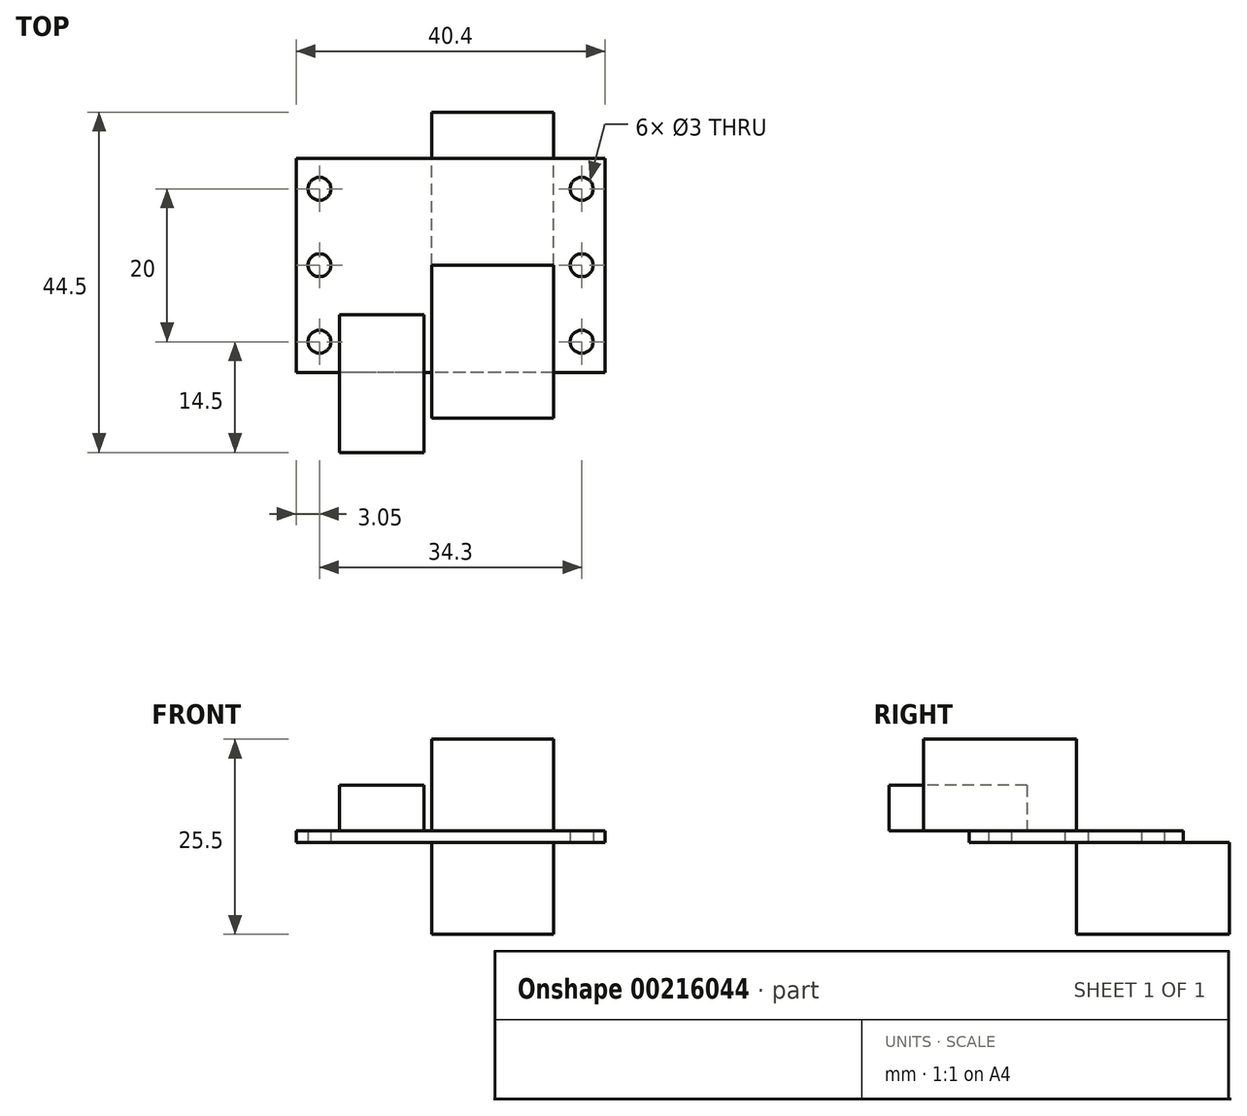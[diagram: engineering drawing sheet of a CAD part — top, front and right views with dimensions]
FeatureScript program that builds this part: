
annotation { "Feature Type Name" : "Feature", "Feature Type Description" : "" }
export const myFeature = defineFeature(function(context is Context, id is Id, definition is map)
    precondition{}
    {
        {
            var Q0;
            Q0=qCreatedBy(makeId("Top.planeOp"),FACE);
            var sketch = newSketch(context, id + "F0", { "sketchPlane" : qUnion([Q0])});
            skLineSegment(sketch, "E0.bottom", {"start": v(20.2, -14) * mm, "end": v(-20.2, -14) * mm});
            skLineSegment(sketch, "E0.top", {"start": v(20.2, 14) * mm, "end": v(-20.2, 14) * mm});
            skLineSegment(sketch, "E0.left", {"start": v(20.2, -14) * mm, "end": v(20.2, 14) * mm});
            skLineSegment(sketch, "E0.right", {"start": v(-20.2, -14) * mm, "end": v(-20.2, 14) * mm});
            skPoint(sketch, "E0.middle", {"position": v(0, 0) * mm});
            skCircle(sketch, "E1", {"center": v(-17.15, 0) * mm, "radius": 1.5 * mm});
            skCircle(sketch, "E2", {"center": v(17.15, 0) * mm, "radius": 1.5 * mm});
            skCircle(sketch, "E3", {"center": v(17.15, 10) * mm, "radius": 1.5 * mm});
            skCircle(sketch, "E4", {"center": v(17.15, -10) * mm, "radius": 1.5 * mm});
            skCircle(sketch, "E5", {"center": v(-17.15, 10) * mm, "radius": 1.5 * mm});
            skCircle(sketch, "E6", {"center": v(-17.15, -10) * mm, "radius": 1.5 * mm});
            skLineSegment(sketch, "E7", {"start": v(0, -9.21) * mm, "end": v(0, 7.96) * mm, "construction": true});
            skLineSegment(sketch, "E8", {"start": v(-9.5, 0) * mm, "end": v(8.49, 0) * mm, "construction": true});
            skSolve(sketch);
        }
        {
            var Q0;
            Q0 = qSketchRegion(id + "F0", true);
            extrude(context, id + "F1", {"entities" : qUnion([Q0]), "depth" : 1.5 * mm});
        }
        {
            var Q0;
            Q0=makeQuery(id+"F1.opExtrude","CAP_FACE",FACE,{"disambiguationData":[OSD([sQuery(id+"F0.wireOp",EDGE,"E0.bottom"),sQuery(id+"F0.wireOp",EDGE,"E0.top"),sQuery(id+"F0.wireOp",EDGE,"E0.left"),sQuery(id+"F0.wireOp",EDGE,"E0.right"),sQuery(id+"F0.wireOp",EDGE,"E1"),sQuery(id+"F0.wireOp",EDGE,"E2"),sQuery(id+"F0.wireOp",EDGE,"E3"),sQuery(id+"F0.wireOp",EDGE,"E4"),sQuery(id+"F0.wireOp",EDGE,"E5"),sQuery(id+"F0.wireOp",EDGE,"E6")])],"isStart":false});
            var sketch = newSketch(context, id + "F2", { "sketchPlane" : qUnion([Q0])});
            skLineSegment(sketch, "E9.bottom", {"start": v(13.5, 0) * mm, "end": v(-2.5, 0) * mm});
            skLineSegment(sketch, "E9.top", {"start": v(13.5, -20) * mm, "end": v(-2.5, -20) * mm});
            skLineSegment(sketch, "E9.left", {"start": v(13.5, -20) * mm, "end": v(13.5, 0) * mm});
            skLineSegment(sketch, "E9.right", {"start": v(-2.5, -20) * mm, "end": v(-2.5, 0) * mm});
            skPoint(sketch, "E9.middle", {"position": v(5.5, -10) * mm});
            skSolve(sketch);
        }
        {
            var Q0;
            Q0 = qSketchRegion(id + "F2", true);
            extrude(context, id + "F3", {"entities" : qUnion([Q0]), "depth" : 12 * mm});
        }
        {
            var Q0;
            Q0=makeQuery(id+"F1.opExtrude","CAP_FACE",FACE,{"disambiguationData":[OSD([sQuery(id+"F0.wireOp",EDGE,"E0.bottom"),sQuery(id+"F0.wireOp",EDGE,"E0.top"),sQuery(id+"F0.wireOp",EDGE,"E0.left"),sQuery(id+"F0.wireOp",EDGE,"E0.right"),sQuery(id+"F0.wireOp",EDGE,"E1"),sQuery(id+"F0.wireOp",EDGE,"E2"),sQuery(id+"F0.wireOp",EDGE,"E3"),sQuery(id+"F0.wireOp",EDGE,"E4"),sQuery(id+"F0.wireOp",EDGE,"E5"),sQuery(id+"F0.wireOp",EDGE,"E6")])],"isStart":true});
            var sketch = newSketch(context, id + "F4", { "sketchPlane" : qUnion([Q0])});
            skLineSegment(sketch, "E10.bottom", {"start": v(-2.5, 0) * mm, "end": v(13.5, 0) * mm});
            skLineSegment(sketch, "E10.top", {"start": v(-2.5, -20) * mm, "end": v(13.5, -20) * mm});
            skLineSegment(sketch, "E10.left", {"start": v(-2.5, 0) * mm, "end": v(-2.5, -20) * mm});
            skLineSegment(sketch, "E10.right", {"start": v(13.5, 0) * mm, "end": v(13.5, -20) * mm});
            skPoint(sketch, "E10.middle", {"position": v(5.5, -10) * mm});
            skSolve(sketch);
        }
        {
            var Q0;
            Q0 = qSketchRegion(id + "F4", true);
            extrude(context, id + "F5", {"entities" : qUnion([Q0]), "depth" : 12 * mm});
        }
        {
            var Q0;
            Q0=makeQuery(id+"F1.opExtrude","CAP_FACE",FACE,{"disambiguationData":[OSD([sQuery(id+"F0.wireOp",EDGE,"E0.bottom"),sQuery(id+"F0.wireOp",EDGE,"E0.top"),sQuery(id+"F0.wireOp",EDGE,"E0.left"),sQuery(id+"F0.wireOp",EDGE,"E0.right"),sQuery(id+"F0.wireOp",EDGE,"E1"),sQuery(id+"F0.wireOp",EDGE,"E2"),sQuery(id+"F0.wireOp",EDGE,"E3"),sQuery(id+"F0.wireOp",EDGE,"E4"),sQuery(id+"F0.wireOp",EDGE,"E5"),sQuery(id+"F0.wireOp",EDGE,"E6")])],"isStart":false});
            var sketch = newSketch(context, id + "F6", { "sketchPlane" : qUnion([Q0])});
            skLineSegment(sketch, "E11.bottom", {"start": v(-14.5, -6.5) * mm, "end": v(-3.5, -6.5) * mm});
            skLineSegment(sketch, "E11.top", {"start": v(-14.5, -24.5) * mm, "end": v(-3.5, -24.5) * mm});
            skLineSegment(sketch, "E11.left", {"start": v(-14.5, -6.5) * mm, "end": v(-14.5, -24.5) * mm});
            skLineSegment(sketch, "E11.right", {"start": v(-3.5, -6.5) * mm, "end": v(-3.5, -24.5) * mm});
            skPoint(sketch, "E11.middle", {"position": v(-9, -15.5) * mm});
            skSolve(sketch);
        }
        {
            var Q0;
            Q0 = qSketchRegion(id + "F6", true);
            extrude(context, id + "F7", {"entities" : qUnion([Q0]), "depth" : 6 * mm});
        }
    });
